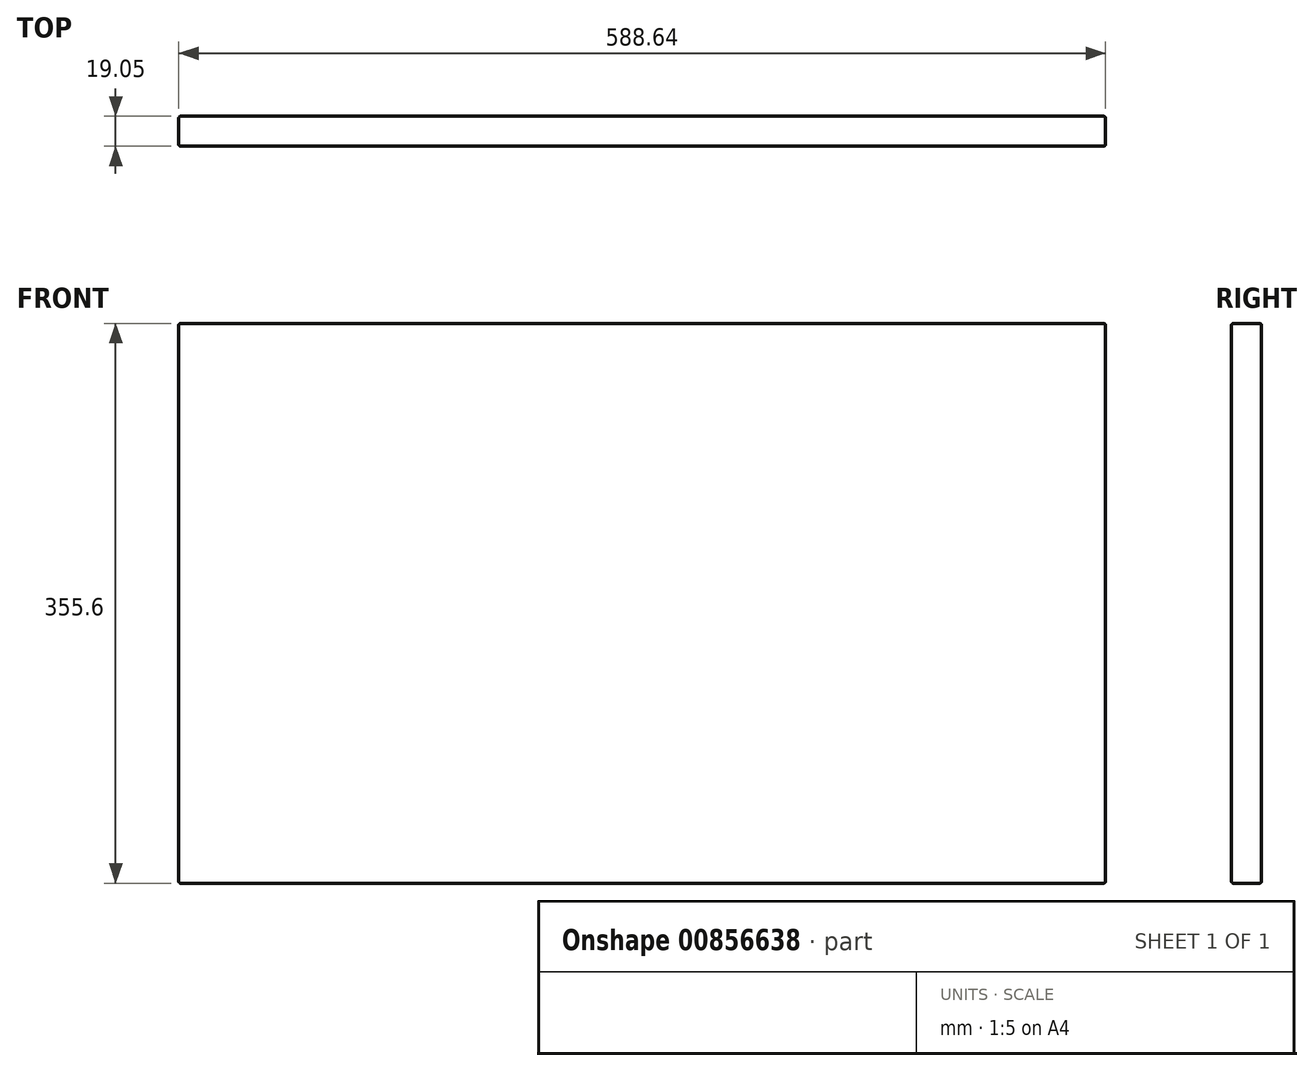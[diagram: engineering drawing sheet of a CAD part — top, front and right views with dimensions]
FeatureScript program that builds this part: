
annotation { "Feature Type Name" : "Feature", "Feature Type Description" : "" }
export const myFeature = defineFeature(function(context is Context, id is Id, definition is map)
    precondition{}
    {
        {
            var Q0;
            Q0=qCreatedBy(makeId("Front.planeOp"),FACE);
            var sketch = newSketch(context, id + "F0", { "sketchPlane" : qUnion([Q0])});
            skLineSegment(sketch, "E0.left", {"start": v(0, 0) * mm, "end": v(0.1, 863.6) * mm});
            skLineSegment(sketch, "E0.right", {"start": v(-1905, -2.15) * mm, "end": v(-1904.9, 861.45) * mm});
            skLineSegment(sketch, "E1.top", {"start": v(0.1, 901.7) * mm, "end": v(-2504.34, 901.7) * mm});
            skLineSegment(sketch, "E1.left", {"start": v(0.1, 863.6) * mm, "end": v(0.1, 901.7) * mm});
            skLineSegment(sketch, "E1.right", {"start": v(-2504.34, 863.6) * mm, "end": v(-2504.34, 901.7) * mm});
            skLineSegment(sketch, "E2", {"start": v(-1904.9, 1058.57) * mm, "end": v(-1904.9, -228.77) * mm, "construction": true});
            skLineSegment(sketch, "E3", {"start": v(0, 1058.57) * mm, "end": v(0, -228.77) * mm, "construction": true});
            skLineSegment(sketch, "E4.bottom", {"start": v(0, 0) * mm, "end": v(-381, 0) * mm});
            skLineSegment(sketch, "E4.left", {"start": v(0, 0) * mm, "end": v(0, 857.25) * mm});
            skLineSegment(sketch, "E5", {"start": v(-381, 0) * mm, "end": v(-387.35, 0) * mm, "construction": true});
            skLineSegment(sketch, "E6.bottom", {"start": v(-387.35, 0) * mm, "end": v(-1143, 0) * mm, "construction": true});
            skLineSegment(sketch, "E6.left", {"start": v(-387.35, 0) * mm, "end": v(-387.35, 736.6) * mm, "construction": true});
            skLineSegment(sketch, "E7", {"start": v(0, 0) * mm, "end": v(-1905, -2.15) * mm, "construction": true});
            skLineSegment(sketch, "E8.bottom", {"start": v(-387.35, 857.25) * mm, "end": v(-1143, 857.25) * mm, "construction": true});
            skLineSegment(sketch, "E8.top", {"start": v(-387.35, 121.5) * mm, "end": v(-1143, 120.65) * mm, "construction": true});
            skLineSegment(sketch, "E8.left", {"start": v(-387.35, 857.25) * mm, "end": v(-387.35, 121.5) * mm, "construction": true});
            skLineSegment(sketch, "E8.right", {"start": v(-1143, 857.25) * mm, "end": v(-1143, 120.65) * mm, "construction": true});
            skLineSegment(sketch, "E9", {"start": v(-1149.35, 857.25) * mm, "end": v(-1149.35, 120.65) * mm, "construction": true});
            skLineSegment(sketch, "E10.bottom", {"start": v(-1149.35, 857.25) * mm, "end": v(-1527.18, 857.25) * mm});
            skLineSegment(sketch, "E10.top", {"start": v(-1149.35, 82.55) * mm, "end": v(-1527.18, 82.55) * mm});
            skLineSegment(sketch, "E10.left", {"start": v(-1149.35, 857.25) * mm, "end": v(-1149.35, 82.55) * mm});
            skLineSegment(sketch, "E10.right", {"start": v(-1527.18, 857.25) * mm, "end": v(-1527.18, 82.55) * mm});
            skLineSegment(sketch, "E11", {"start": v(-1527.18, 82.55) * mm, "end": v(-1533.53, 82.54) * mm, "construction": true});
            skLineSegment(sketch, "E12.bottom", {"start": v(-1533.53, 82.54) * mm, "end": v(-1911.35, 82.54) * mm});
            skLineSegment(sketch, "E12.top", {"start": v(-1533.53, 857.25) * mm, "end": v(-1911.35, 857.25) * mm});
            skLineSegment(sketch, "E12.left", {"start": v(-1533.53, 82.54) * mm, "end": v(-1533.53, 857.25) * mm});
            skLineSegment(sketch, "E12.right", {"start": v(-1911.35, 82.54) * mm, "end": v(-1911.35, 857.25) * mm});
            skLineSegment(sketch, "E13", {"start": v(0, 857.25) * mm, "end": v(-2682.58, 857.25) * mm, "construction": true});
            skLineSegment(sketch, "E14.bottom", {"start": v(0, 857.25) * mm, "end": v(-381, 857.25) * mm});
            skLineSegment(sketch, "E14.top", {"start": v(0, 82.55) * mm, "end": v(-381, 82.55) * mm});
            skLineSegment(sketch, "E14.left", {"start": v(0, 857.25) * mm, "end": v(0, 82.55) * mm});
            skLineSegment(sketch, "E14.right", {"start": v(-381, 857.25) * mm, "end": v(-381, 82.55) * mm});
            skLineSegment(sketch, "E15.bottom", {"start": v(-387.35, 82.55) * mm, "end": v(-1143, 82.55) * mm});
            skLineSegment(sketch, "E15.top", {"start": v(-387.35, 115.22) * mm, "end": v(-1143, 115.22) * mm});
            skLineSegment(sketch, "E15.left", {"start": v(-387.35, 82.55) * mm, "end": v(-387.35, 115.22) * mm});
            skLineSegment(sketch, "E15.right", {"start": v(-1143, 82.55) * mm, "end": v(-1143, 115.22) * mm});
            skPoint(sketch, "E16", {"position": v(-765.18, 121.08) * mm});
            skPoint(sketch, "E17", {"position": v(-1530.35, 82.55) * mm});
            skPoint(sketch, "E17.positionSnap0", {"position": v(-1530.35, 82.55) * mm});
            skLineSegment(sketch, "E18", {"start": v(-765.18, 121.08) * mm, "end": v(-765.18, 1778) * mm, "construction": true});
            skPoint(sketch, "E19.middle", {"position": v(-765.18, 1778) * mm});
            skLineSegment(sketch, "E20.bottom", {"start": v(-2504.34, 2133.6) * mm, "end": v(-1915.7, 2133.6) * mm});
            skLineSegment(sketch, "E20.top", {"start": v(-2504.34, 1778) * mm, "end": v(-1915.7, 1778) * mm});
            skLineSegment(sketch, "E20.left", {"start": v(-2504.34, 2133.6) * mm, "end": v(-2504.34, 1778) * mm});
            skLineSegment(sketch, "E21", {"start": v(-1915.7, 2133.6) * mm, "end": v(-1915.7, 1778) * mm});
            skSolve(sketch);
        }
        {
            var Q0;
            Q0=makeQuery(id+"F0.imprint","IMPRINT",FACE,{"disambiguationData":[TD([[makeQuery(id+"F0.imprint","IMPRINT",EDGE,{"derivedFrom":sQuery(id+"F0.wireOp",EDGE,"E20.bottom")}),-1.0]])]});
            extrude(context, id + "F1", {"entities" : qUnion([Q0]), "depth" : 19.05 * mm, "offsetDistance" : 25.4 * mm});
        }
        {
            var Q0;
            Q0=makeQuery(id+"F1.opExtrude","CAP_FACE",FACE,{"disambiguationData":[OSD([sQuery(id+"F0.wireOp",EDGE,"E20.bottom"),sQuery(id+"F0.wireOp",EDGE,"E20.top"),sQuery(id+"F0.wireOp",EDGE,"E20.left"),sQuery(id+"F0.wireOp",EDGE,"E21")])],"isStart":false});
            var Q1;
            Q1=makeQuery(id+"F1.opExtrude","SWEPT_FACE",FACE,{"disambiguationData":[OSD([sQuery(id+"F0.wireOp",EDGE,"E20.bottom")])]});
            var Q2;
            Q2=makeQuery(id+"F1.opExtrude","SWEPT_FACE",FACE,{"disambiguationData":[OSD([sQuery(id+"F0.wireOp",EDGE,"E20.left")])]});
            var Q3;
            Q3=makeQuery(id+"F1.opExtrude","SWEPT_FACE",FACE,{"disambiguationData":[OSD([sQuery(id+"F0.wireOp",EDGE,"E21")])]});
            var Q4;
            Q4=makeQuery(id+"F1.opExtrude","CAP_EDGE",EDGE,{"disambiguationData":[OSD([sQuery(id+"F0.wireOp",EDGE,"E20.top")])],"isStart":true});
            fillet(context, id + "F2", {"entities" : qUnion([Q0, Q1, Q2, Q3, Q4]), "radius" : 1.27 * mm, "tangentPropagation" : true, "allowEdgeOverflow" : false});
        }
    });
